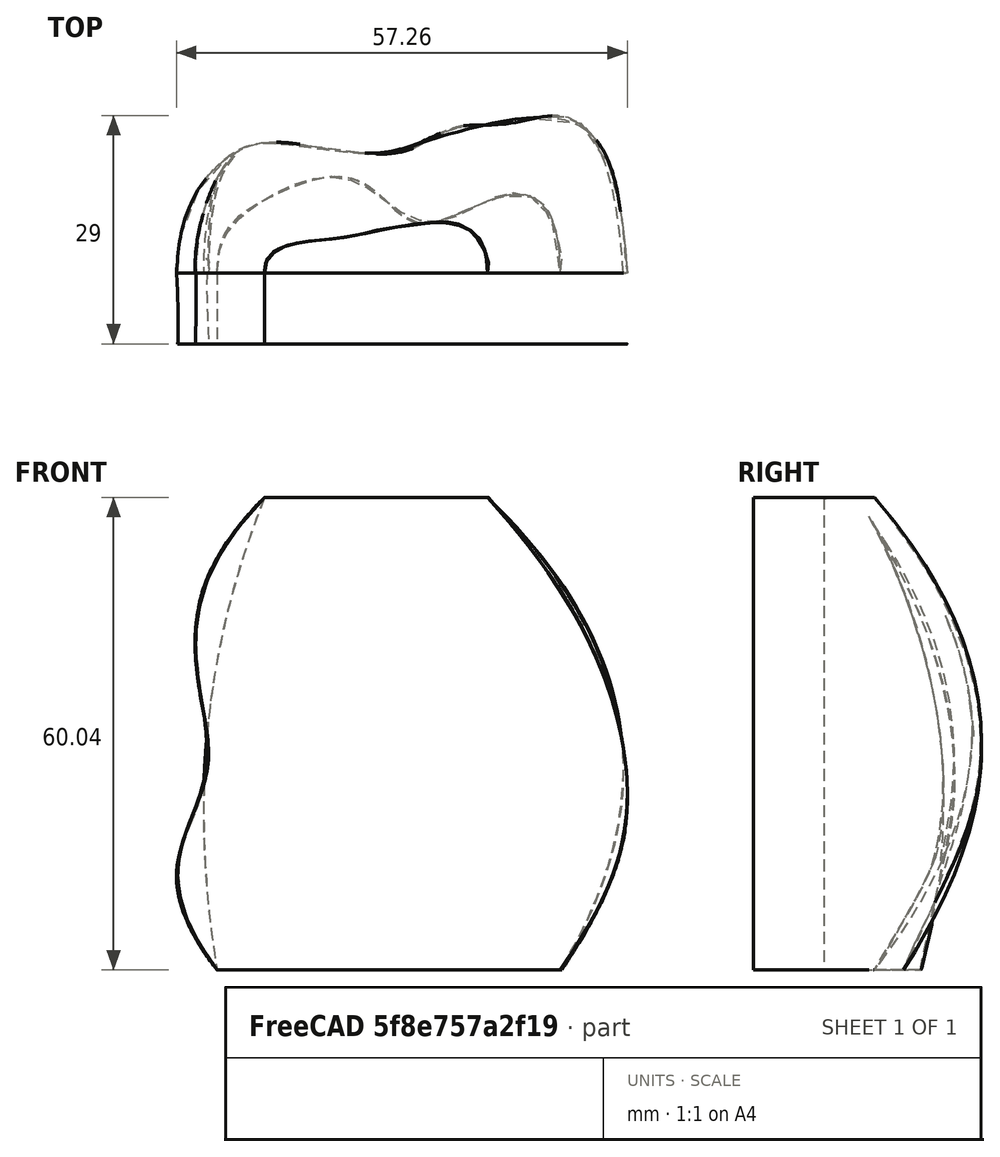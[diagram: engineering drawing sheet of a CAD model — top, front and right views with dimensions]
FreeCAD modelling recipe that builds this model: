
FCSTD DOCUMENT  (FreeCAD 0.17R12865 (Git))
Label: Gordon-1
License: All rights reserved
LicenseURL: http://en.wikipedia.org/wiki/All_rights_reserved
objects: Sketcher::SketchObject×5, Part::Feature×4, Part::RuledSurface×2, Part::Loft×1, App::FeaturePython×1, Part::FeaturePython×1
note: 14 computed .brp shape members not serialized (recipe doc carries the construction recipe); baked Part::Feature solids carry a one-line shape summary decoded from their .brp

FEATURE [Sketcher::SketchObject] Sketch006
  MapMode = 5
  sketch-geometry (15):
    g0-g7: Circle [constr] x8 (B-spline internal-alignment scaffolding for g8; pole/knot coordinates omitted)
    g8: BSplineCurve PolesCount=8 KnotsCount=6 Degree=3 IsPeriodic=0
    g9-g14: GeomPoint [constr] x6 (B-spline internal-alignment scaffolding for g8; pole/knot coordinates omitted)
  constraints (6):
    c: Coincident(g0,g-3)
    c: Radius(g0) = 1
    c: Equal(g0, g1-g7) x7
    c: Coincident(g7,g-4)
    c: InternalAlignment(g0-g7 -> g8) x8
    c: InternalAlignment(g9-g14 -> g8) x6
FEATURE [Sketcher::SketchObject] Sketch002
  MapMode = 5
  Placement = pos=(0,0,-30) rot=(0,0,1;0rad)
  sketch-geometry (15):
    g0-g7: Circle [constr] x8 (B-spline internal-alignment scaffolding for g8; pole/knot coordinates omitted)
    g8: BSplineCurve PolesCount=8 KnotsCount=6 Degree=3 IsPeriodic=0
    g9-g14: GeomPoint [constr] x6 (B-spline internal-alignment scaffolding for g8; pole/knot coordinates omitted)
  constraints (6):
    c: PointOnObject(g0,g-1)
    c: Radius(g0) = 1
    c: Equal(g0, g1-g7) x7
    c: PointOnObject(g7,g-1)
    c: InternalAlignment(g0-g7 -> g8) x8
    c: InternalAlignment(g9-g14 -> g8) x6
FEATURE [Sketcher::SketchObject] Sketch
  MapMode = 5
  Placement = pos=(0,0,30) rot=(0,0,1;0rad)
  sketch-geometry (11):
    g0-g5: Circle [constr] x6 (B-spline internal-alignment scaffolding for g6; pole/knot coordinates omitted)
    g6: BSplineCurve PolesCount=6 KnotsCount=4 Degree=3 IsPeriodic=0
    g7-g10: GeomPoint [constr] x4 (B-spline internal-alignment scaffolding for g6; pole/knot coordinates omitted)
  constraints (6):
    c: PointOnObject(g0,g-1)
    c: Radius(g0) = 1
    c: Equal(g0, g1-g5) x5
    c: PointOnObject(g5,g-1)
    c: InternalAlignment(g0-g5 -> g6) x6
    c: InternalAlignment(g7-g10 -> g6) x4
FEATURE [Sketcher::SketchObject] Sketch003
  ExternalGeometry = -> [Sketch,Sketch002]
  MapMode = 5
  Placement = pos=(0,0,0) rot=(1,0,0;1.5708rad)
  sketch-geometry (9):
    g0-g4: Circle [constr] x5 (B-spline internal-alignment scaffolding for g5; pole/knot coordinates omitted)
    g5: BSplineCurve PolesCount=5 KnotsCount=3 Degree=3 IsPeriodic=0
    g6: GeomPoint [constr] X=-14.2283 Y=30 Z=0
    g7: GeomPoint [constr] X=-21.3831 Y=-3.30814 Z=0
    g8: GeomPoint [constr] X=-20.2931 Y=-30 Z=0
  constraints (8):
    c: Coincident(g0,g-3)
    c: Radius(g0) = 3
    c: Equal(g0, g1-g4) x4
    c: Coincident(g4,g-4)
    c: InternalAlignment(g0-g4 -> g5) x5
    c: InternalAlignment(g6,g5)
    c: InternalAlignment(g7,g5)
    c: InternalAlignment(g8,g5)
FEATURE [Sketcher::SketchObject] Sketch004
  ExternalGeometry = -> [Sketch,Sketch002]
  MapMode = 5
  Placement = pos=(0,0,0) rot=(1,0,0;1.5708rad)
  sketch-geometry (9):
    g0-g4: Circle [constr] x5 (B-spline internal-alignment scaffolding for g5; pole/knot coordinates omitted)
    g5: BSplineCurve PolesCount=5 KnotsCount=3 Degree=3 IsPeriodic=0
    g6: GeomPoint [constr] X=14.0666 Y=30 Z=0
    g7: GeomPoint [constr] X=31.3555 Y=-1.98124 Z=0
    g8: GeomPoint [constr] X=23.2471 Y=-30 Z=0
  constraints (8):
    c: Coincident(g0,g-3)
    c: Radius(g0) = 3
    c: Equal(g0, g1-g4) x4
    c: InternalAlignment(g0-g4 -> g5) x5
    c: InternalAlignment(g6,g5)
    c: InternalAlignment(g7,g5)
    c: InternalAlignment(g8,g5)
    c: Coincident(g4,g-4)
FEATURE [Part::RuledSurface] Ruled_Surface
  Curve1 = -> Sketch003
  Curve2 = -> Sketch004
  Orientation = 0
FEATURE [Part::Loft] Loft
  Closed = false
  MaxDegree = 3
  Ruled = false
  Sections = -> [Sketch,Sketch006,Sketch002]
  Solid = false
FEATURE [Part::Feature] Shape  label="InterPts"
  shape: bbox 58.11 x 2e-07 x 60 mm, 1 faces, 0 solids (baked)
FEATURE [App::FeaturePython] Sweep_2_rails  # WARN: FeaturePython — macro-defined, semantics opaque (R4)
  Birail = -> Ruled_Surface
  Blending = 1
  Extend = false
  Parametrization = 0
  Points = (400) [(-14.2283,7.88861e-31,30),(-13.9202,1.77412,30),(-12.5851,2.99068,30),(-10.8707,3.61798,30),(-9.07283,3.95839,30),(-7.25488,4.17295,30),+394 more]
  ProfileSamples = 20
  Profiles = -> [Sketch,Sketch006,Sketch002]
  RailSamples = 20
FEATURE [Part::Feature] Shape001
  shape: bbox 57.31 x 20.31 x 60 mm, 1 faces, 0 solids (baked)
FEATURE [Part::Feature] Shape002
  shape: bbox 57.16 x 20.01 x 60.12 mm, 1 faces, 0 solids (baked)
FEATURE [Part::Feature] Ruled_Surface_Face1
  Placement = pos=(0,-9,0) rot=(0,0,1;0rad)
  shape: bbox 65.22 x 2e-07 x 60 mm, 1 faces, 0 solids (baked)
FEATURE [Part::FeaturePython] Approximation_Curve  # WARN: FeaturePython — macro-defined, semantics opaque (R4)
  ApproxTolerance = 0.5
  ClampEnds = false
  Continuity = 3
  CurvatureWeight = 1
  DegreeMax = 5
  DegreeMin = 3
  FirstIndex = 0
  LastIndex = 19
  LengthWeight = 1
  Method = 0
  Parametrization = 0
  PointObject = -> Sweep_2_rails
  TorsionWeight = 1
FEATURE [Part::RuledSurface] Ruled_Surface001
  Curve1 = -> Approximation_Curve [Edge2]
  Curve2 = -> Ruled_Surface_Face1 [Edge1]
  Orientation = 0
